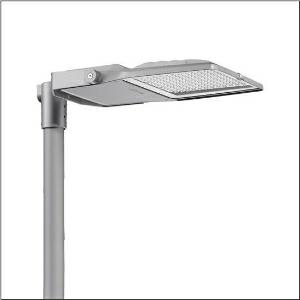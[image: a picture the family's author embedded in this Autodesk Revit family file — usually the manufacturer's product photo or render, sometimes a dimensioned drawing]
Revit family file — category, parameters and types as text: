
# Revit family: floodlight_fl_21_midi___pl43_5xa7786f2a3a_0f3f
name_source: partatom
category: Lighting Fixtures
units: mm (PartAtom-declared; Revit-internal decimal feet)

## family parameters
Cut with Voids When Loaded = No
Host = Face
Light Source = No
Part Type = Normal
Room Calculation Point = No
Round Connector Dimension = Use Diameter
Shared = No

## types (1)
- --- (1 x LED, 36680 lm, 271.6 W, 3000K)
    Apparent Load = 272 VA
    CIE Flux Codes = 27 78 99 100 100
    Color Rendering = 70
    Color Temperature = 3000K
    Default Elevation = 1800 mm
    Description = Floodlight FL 21 midi, floodlight, primary light control with lens, of PMMA, primary optical cover: protective disc, of toughened safety glass, transparent, light distribution: PL43, light emission: direct distribution, installation type: surface-mounted, LED, High Power LED, rated luminous flux: 36.680lm, luminous efficacy: 135lm/W, light colour: 730, colour temperature: 3000K, control gear: Smart Interface (Zhaga), control: flexible luminous flux parameterisation, time-dependent luminous flux control, constant luminous flux control, overheat protection, pre-setting: logarithmic dimming characteristic, with terminal, 6-pole, mains connection: 220..240V, AC, 50/60Hz, start of lifetime: 272W, end of service life: 287W, reduction: 123W, luminaire housing, of diecast aluminium, powder-coated, Siteco® metallic grey (DB 702S), corrosivity category C5 mid according to DIN EN ISO 12944, suitable for swimming pools, chlorine-resistant, sealing non-destructively replaceable, please order mast flange separately, mast bracket, of steel, galvanised, powder-coated, Siteco® metallic grey (DB 702S), Smart Interface below and above, protection rating (complete): IP66, insulation class (complete): insulation class II (safety insulation), certification: CE, ENEC, VDE, protection symbol: D, impact resistance: IK08, permissible operating ambient temperature: -40..+40°C, permissible operating ambient temperature for outdoor applications: -40..+50°C, standard: DIN EN 12944, LABS conformity tested according to VDMA 24364:2018-05, packaging unit: 1 piece

Light Distribution: PL43
    Height = 76 mm
    Lamp = 1 x LED
    Lamp Light Flux = 36680 lm
    Lamp Power = 271.6 W
    Lamp count = 1
    Length = 657 mm
    Luminous efficacy = 135 lm/W
    Manufacturer = Siteco
    ModVariant = No
    Model = 5XA7786F2A3A
    Number of Poles = 1
    OnlyDefault = Yes
    Power Factor = 1
    Product Name = Floodlight FL 21 midi | PL43
    Product group = floodlight | pylon annexe
    ProductGroupID = 6200
    Protection Class = Protection class II
    Protection Degree = IP 66
    RLX_Detail_Level = 1
    RLX_Emergency_Light_Flux = 0 lm
    RLX_Emergency_Type = 0
    RLX_Emergency_Type_DB = No
    RlxData = <blob elided: 153397 chars, md5=c15504d9>
    Socket = socket
    Standby Power = 0 W
    System Light Flux = 36680 lm
    System Power = 272 W
    Type Comments = factory setting: luminous flux: 100 % | dim-lin: 254 | 620 mA
    Type Image = l_1007123.jpg
    URL = http://relux.com
    VarID = @adj_177098
    Voltage = 0 V
    Weight = 0.00 kg
    Width = 442 mm

## geometry (parser evidence)
native form markers: Blend x4, Sweep x13
no freeform markers — native parametric forms only
